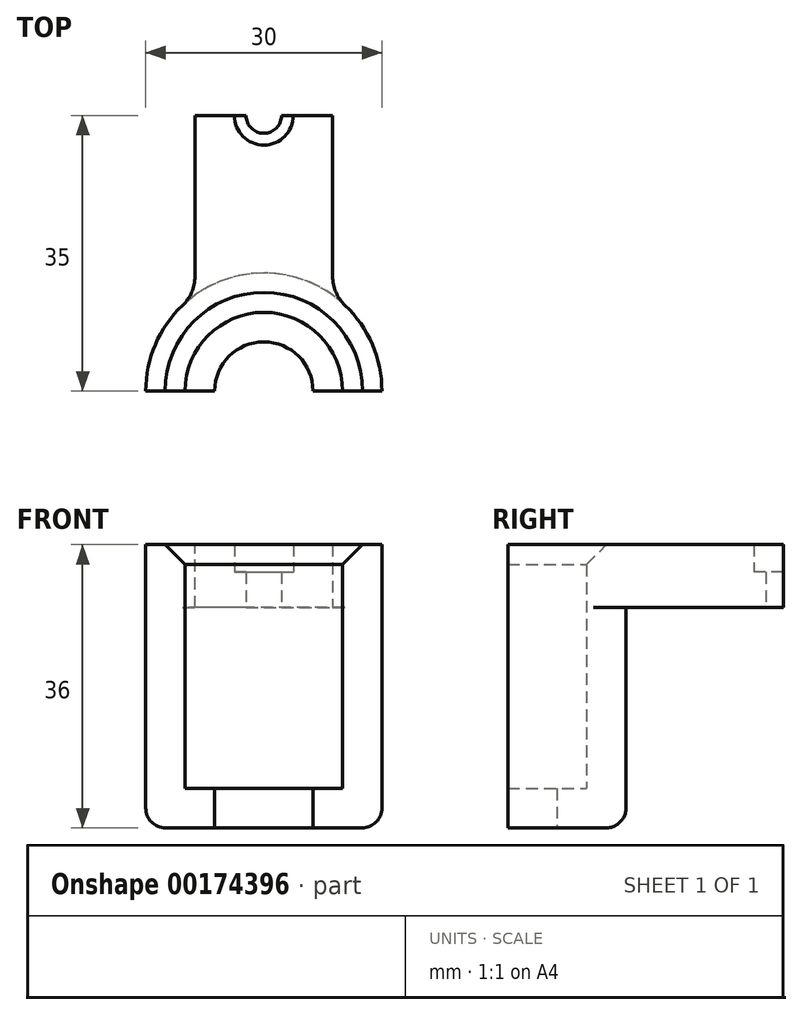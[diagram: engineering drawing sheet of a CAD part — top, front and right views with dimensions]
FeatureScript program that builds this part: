
annotation { "Feature Type Name" : "Feature", "Feature Type Description" : "" }
export const myFeature = defineFeature(function(context is Context, id is Id, definition is map)
    precondition{}
    {
        {
            var Q0;
            Q0=qCreatedBy(makeId("Top.planeOp"),FACE);
            var sketch = newSketch(context, id + "F0", { "sketchPlane" : qUnion([Q0])});
            skCircle(sketch, "E0", {"center": v(0, 0) * mm, "radius": 10 * mm});
            skCircle(sketch, "E1", {"center": v(0, 0) * mm, "radius": 15 * mm});
            skLineSegment(sketch, "E2", {"start": v(0, 0) * mm, "end": v(-10, 0) * mm});
            skLineSegment(sketch, "E3", {"start": v(-10, 0) * mm, "end": v(-15, 0) * mm});
            skLineSegment(sketch, "E4", {"start": v(0, 0) * mm, "end": v(10, 0) * mm});
            skLineSegment(sketch, "E5", {"start": v(10, 0) * mm, "end": v(15, 0) * mm});
            skCircle(sketch, "E6", {"center": v(0, 0) * mm, "radius": 6.25 * mm});
            skSolve(sketch);
        }
        {
            var Q0;
            {var subQ0=sQuery(id+"F0.wireOp",EDGE,"E2");var subQ5=sQuery(id+"F0.wireOp",EDGE,"E6");var subQ6=makeQuery(id+"F0.imprint","INTERSECT",VERTEX,{"derivedFrom":[subQ0,subQ5]});Q0=makeQuery(id+"F0.imprint","IMPRINT",FACE,{"disambiguationData":[TD([[makeQuery(id+"F0.imprint","IMPRINT",EDGE,{"disambiguationData":[TD([[subQ6,1.0]])],"derivedFrom":subQ5}),-1.0]])]});}
            extrude(context, id + "F1", {"entities" : qUnion([Q0]), "depth" : 2 * mm});
        }
        {
            var Q0;
            {var subQ0=sQuery(id+"F0.wireOp",EDGE,"E3");Q0=makeQuery(id+"F0.imprint","IMPRINT",FACE,{"disambiguationData":[TD([[makeQuery(id+"F0.imprint","IMPRINT",EDGE,{"derivedFrom":subQ0}),-1.0]])]});}
            extrude(context, id + "F2", {"entities" : qUnion([Q0]), "operationType" : NewBodyOperationType.ADD, "depth" : 25 * mm});
        }
        {
            var Q0;
            Q0=makeQuery(id+"F2.opExtrude","CAP_FACE",FACE,{"disambiguationData":[OSD([sQuery(id+"F0.wireOp",EDGE,"E0"),sQuery(id+"F0.wireOp",EDGE,"E1"),sQuery(id+"F0.wireOp",EDGE,"E3"),sQuery(id+"F0.wireOp",EDGE,"E5")])],"isStart":false});
            var sketch = newSketch(context, id + "F3", { "sketchPlane" : qUnion([Q0])});
            skLineSegment(sketch, "E7", {"start": v(0, 0) * mm, "end": v(0, 15) * mm});
            skLineSegment(sketch, "E8", {"start": v(0, 15) * mm, "end": v(0, 35) * mm});
            skCircle(sketch, "E9", {"center": v(0, 35) * mm, "radius": 3.75 * mm});
            skCircle(sketch, "E10", {"center": v(0, 35) * mm, "radius": 8.75 * mm});
            skLineSegment(sketch, "E11", {"start": v(0, 35) * mm, "end": v(-8.75, 35) * mm});
            skLineSegment(sketch, "E12", {"start": v(-8.75, 35) * mm, "end": v(8.75, 35) * mm});
            skLineSegment(sketch, "E13", {"start": v(8.75, 35) * mm, "end": v(8.75, 0) * mm});
            skLineSegment(sketch, "E14", {"start": v(-8.75, 35) * mm, "end": v(-8.75, 0) * mm});
            skLineSegment(sketch, "E15", {"start": v(-8.75, 0) * mm, "end": v(0, 0) * mm});
            skLineSegment(sketch, "E16", {"start": v(8.75, 0) * mm, "end": v(0, 0) * mm});
            skCircle(sketch, "E17", {"center": v(0, 0) * mm, "radius": 10 * mm});
            skCircle(sketch, "E18", {"center": v(0, 0) * mm, "radius": 15 * mm});
            skLineSegment(sketch, "E19", {"start": v(0, 0) * mm, "end": v(-15, 0) * mm});
            skLineSegment(sketch, "E20", {"start": v(-15, 0) * mm, "end": v(15, 0) * mm});
            skCircle(sketch, "E21", {"center": v(0, 35) * mm, "radius": 2.25 * mm});
            skSolve(sketch);
        }
        {
            var Q0;
            {var subQ1=sQuery(id+"F3.wireOp",EDGE,"E8");var subQ3=sQuery(id+"F3.wireOp",EDGE,"E10");var subQ4=makeQuery(id+"F3.imprint","INTERSECT",VERTEX,{"derivedFrom":[subQ1,subQ3]});Q0=makeQuery(id+"F3.imprint","IMPRINT",FACE,{"disambiguationData":[TD([[makeQuery(id+"F3.imprint","IMPRINT",EDGE,{"disambiguationData":[TD([[subQ4,1.0]])],"derivedFrom":subQ1}),1.0]])]});}
            var Q1;
            {var subQ1=sQuery(id+"F3.wireOp",EDGE,"E8");var subQ3=sQuery(id+"F3.wireOp",EDGE,"E10");var subQ4=makeQuery(id+"F3.imprint","INTERSECT",VERTEX,{"derivedFrom":[subQ1,subQ3]});Q1=makeQuery(id+"F3.imprint","IMPRINT",FACE,{"disambiguationData":[TD([[makeQuery(id+"F3.imprint","IMPRINT",EDGE,{"disambiguationData":[TD([[subQ4,1.0]])],"derivedFrom":subQ1}),-1.0]])]});}
            var Q2;
            {var subQ0=sQuery(id+"F3.wireOp",EDGE,"E12");var subQ1=sQuery(id+"F3.wireOp",EDGE,"E9");var subQ2=makeQuery(id+"F3.imprint","INTERSECT",VERTEX,{"disambiguationData":[OD(0.0)],"derivedFrom":[subQ1,subQ0]});Q2=makeQuery(id+"F3.imprint","IMPRINT",FACE,{"disambiguationData":[TD([[makeQuery(id+"F3.imprint","IMPRINT",EDGE,{"disambiguationData":[TD([[subQ2,1.0]])],"derivedFrom":subQ1}),-1.0]])]});}
            var Q3;
            {var subQ0=sQuery(id+"F3.wireOp",EDGE,"E18");var subQ1=sQuery(id+"F3.wireOp",EDGE,"E13");var subQ2=makeQuery(id+"F3.imprint","INTERSECT",VERTEX,{"derivedFrom":[subQ1,subQ0]});Q3=makeQuery(id+"F3.imprint","IMPRINT",FACE,{"disambiguationData":[TD([[makeQuery(id+"F3.imprint","IMPRINT",EDGE,{"disambiguationData":[TD([[subQ2,-1.0]])],"derivedFrom":subQ1}),1.0]])]});}
            var Q4;
            {var subQ0=sQuery(id+"F3.wireOp",EDGE,"E18");var subQ1=sQuery(id+"F3.wireOp",EDGE,"E14");var subQ2=makeQuery(id+"F3.imprint","INTERSECT",VERTEX,{"derivedFrom":[subQ1,subQ0]});Q4=makeQuery(id+"F3.imprint","IMPRINT",FACE,{"disambiguationData":[TD([[makeQuery(id+"F3.imprint","IMPRINT",EDGE,{"disambiguationData":[TD([[subQ2,-1.0]])],"derivedFrom":subQ1}),-1.0]])]});}
            var Q5;
            {var subQ0=sQuery(id+"F3.wireOp",EDGE,"E18");var subQ5=sQuery(id+"F3.wireOp",EDGE,"E13");var subQ6=makeQuery(id+"F3.imprint","INTERSECT",VERTEX,{"derivedFrom":[subQ5,subQ0]});Q5=makeQuery(id+"F3.imprint","IMPRINT",FACE,{"disambiguationData":[TD([[makeQuery(id+"F3.imprint","IMPRINT",EDGE,{"disambiguationData":[TD([[subQ6,-1.0]])],"derivedFrom":subQ5}),-1.0]])]});}
            var Q6;
            {var subQ0=sQuery(id+"F3.wireOp",EDGE,"E18");var subQ5=sQuery(id+"F3.wireOp",EDGE,"E14");var subQ7=makeQuery(id+"F3.imprint","INTERSECT",VERTEX,{"derivedFrom":[subQ5,subQ0]});Q6=makeQuery(id+"F3.imprint","IMPRINT",FACE,{"disambiguationData":[TD([[makeQuery(id+"F3.imprint","IMPRINT",EDGE,{"disambiguationData":[TD([[subQ7,-1.0]])],"derivedFrom":subQ5}),1.0]])]});}
            var Q7;
            {var subQ0=sQuery(id+"F3.wireOp",EDGE,"E10");var subQ1=sQuery(id+"F3.wireOp",EDGE,"E8");var subQ2=makeQuery(id+"F3.imprint","INTERSECT",VERTEX,{"derivedFrom":[subQ1,subQ0]});Q7=makeQuery(id+"F3.imprint","IMPRINT",FACE,{"disambiguationData":[TD([[makeQuery(id+"F3.imprint","IMPRINT",EDGE,{"disambiguationData":[TD([[subQ2,-1.0]])],"derivedFrom":subQ1}),1.0]])]});}
            var Q8;
            {var subQ0=sQuery(id+"F3.wireOp",EDGE,"E10");var subQ1=sQuery(id+"F3.wireOp",EDGE,"E8");var subQ2=makeQuery(id+"F3.imprint","INTERSECT",VERTEX,{"derivedFrom":[subQ1,subQ0]});Q8=makeQuery(id+"F3.imprint","IMPRINT",FACE,{"disambiguationData":[TD([[makeQuery(id+"F3.imprint","IMPRINT",EDGE,{"disambiguationData":[TD([[subQ2,-1.0]])],"derivedFrom":subQ1}),-1.0]])]});}
            extrude(context, id + "F4", {"entities" : qUnion([Q0, Q1, Q2, Q3, Q4, Q5, Q6, Q7, Q8]), "operationType" : NewBodyOperationType.ADD, "depth" : 8 * mm});
        }
        {
            var Q0;
            {var subQ0=sQuery(id+"F3.wireOp",EDGE,"E12");var subQ1=sQuery(id+"F3.wireOp",EDGE,"E9");var subQ2=makeQuery(id+"F3.imprint","INTERSECT",VERTEX,{"disambiguationData":[OD(0.0)],"derivedFrom":[subQ1,subQ0]});Q0=makeQuery(id+"F3.imprint","IMPRINT",FACE,{"disambiguationData":[TD([[makeQuery(id+"F3.imprint","IMPRINT",EDGE,{"disambiguationData":[TD([[subQ2,1.0]])],"derivedFrom":subQ1}),1.0]])]});}
            var Q1;
            {var subQ0=sQuery(id+"F3.wireOp",EDGE,"E9");var subQ1=sQuery(id+"F3.wireOp",EDGE,"E8");var subQ2=makeQuery(id+"F3.imprint","INTERSECT",VERTEX,{"derivedFrom":[subQ1,subQ0]});Q1=makeQuery(id+"F3.imprint","IMPRINT",FACE,{"disambiguationData":[TD([[makeQuery(id+"F3.imprint","IMPRINT",EDGE,{"disambiguationData":[TD([[subQ2,-1.0]])],"derivedFrom":subQ1}),1.0]])]});}
            var Q2;
            {var subQ0=sQuery(id+"F3.wireOp",EDGE,"E9");var subQ1=sQuery(id+"F3.wireOp",EDGE,"E8");var subQ2=makeQuery(id+"F3.imprint","INTERSECT",VERTEX,{"derivedFrom":[subQ1,subQ0]});Q2=makeQuery(id+"F3.imprint","IMPRINT",FACE,{"disambiguationData":[TD([[makeQuery(id+"F3.imprint","IMPRINT",EDGE,{"disambiguationData":[TD([[subQ2,-1.0]])],"derivedFrom":subQ1}),-1.0]])]});}
            extrude(context, id + "F5", {"entities" : qUnion([Q0, Q1, Q2]), "operationType" : NewBodyOperationType.ADD, "depth" : 4.5 * mm});
        }
        {
            var Q0;
            Q0=makeQuery(id+"F4.opExtrude","SWEPT_EDGE",EDGE,{"disambiguationData":[OSD([sQuery(id+"F3.wireOp",EDGE,"E14"),sQuery(id+"F3.wireOp",EDGE,"E18")])]});
            var Q1;
            Q1=makeQuery(id+"F4.opExtrude","SWEPT_EDGE",EDGE,{"disambiguationData":[OSD([sQuery(id+"F3.wireOp",EDGE,"E13"),sQuery(id+"F3.wireOp",EDGE,"E18")])]});
            fillet(context, id + "F6", {"entities" : qUnion([Q0, Q1]), "radius" : 5.08 * mm, "tangentPropagation" : true, "allowEdgeOverflow" : false});
        }
        {
            var Q0;
            {var subQ0=sQuery(id+"F0.wireOp",EDGE,"E0");Q0=makeQuery(id+"F2.boolean.opBoolean","MERGE",FACE,{"derivedFrom":[makeQuery(id+"F1.opExtrude","CAP_FACE",FACE,{"disambiguationData":[OSD([subQ0,sQuery(id+"F0.wireOp",EDGE,"E2"),sQuery(id+"F0.wireOp",EDGE,"E4"),sQuery(id+"F0.wireOp",EDGE,"E6")])],"isStart":true}),makeQuery(id+"F2.opExtrude","CAP_FACE",FACE,{"disambiguationData":[OSD([subQ0,sQuery(id+"F0.wireOp",EDGE,"E1"),sQuery(id+"F0.wireOp",EDGE,"E3"),sQuery(id+"F0.wireOp",EDGE,"E5")])],"isStart":true})]});}
            extrude(context, id + "F7", {"entities" : qUnion([Q0]), "operationType" : NewBodyOperationType.ADD, "depth" : 3 * mm});
        }
        {
            var Q0;
            Q0=makeQuery(id+"F7.opExtrude","CAP_EDGE",EDGE,{"disambiguationData":[OSD([sQuery(id+"F0.wireOp",EDGE,"E1")])],"isStart":false});
            fillet(context, id + "F8", {"entities" : qUnion([Q0]), "radius" : 2.54 * mm, "tangentPropagation" : true, "allowEdgeOverflow" : false});
        }
        {
            var Q0;
            Q0=makeQuery(id+"F4.opExtrude","CAP_EDGE",EDGE,{"disambiguationData":[OSD([sQuery(id+"F3.wireOp",EDGE,"E17")])],"isStart":false});
            chamfer(context, id + "F9", {"entities" : qUnion([Q0]), "width" : 2.54 * mm, "tangentPropagation" : true});
        }
    });
